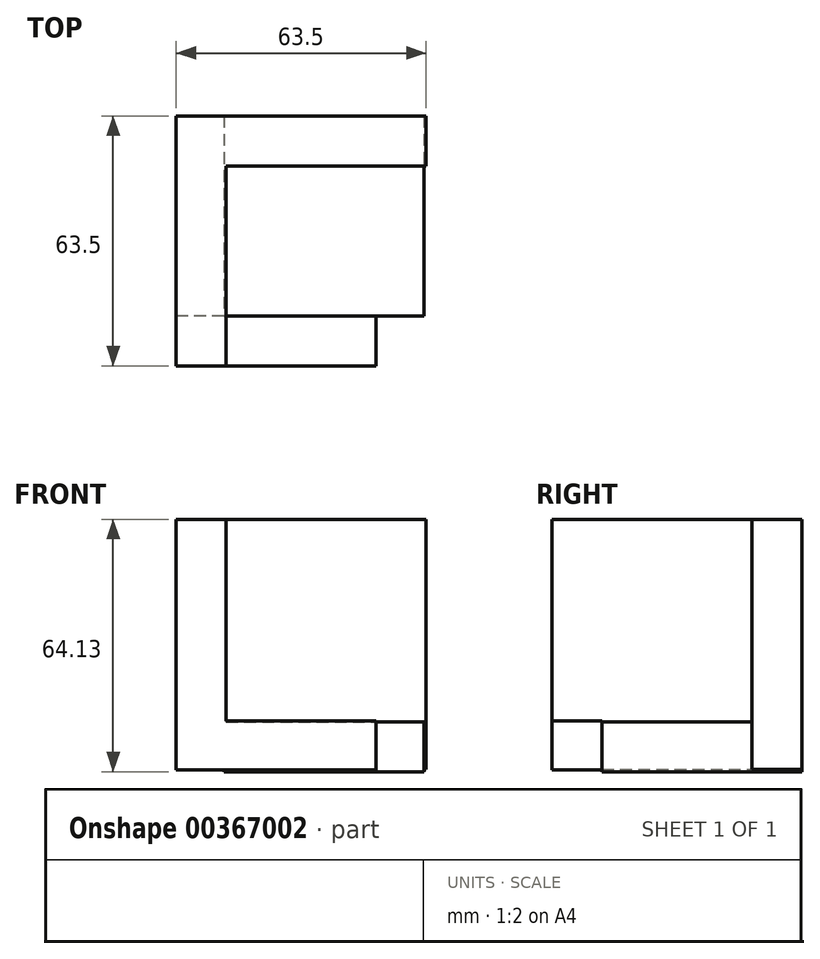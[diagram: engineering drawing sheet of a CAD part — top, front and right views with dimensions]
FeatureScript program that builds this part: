
annotation { "Feature Type Name" : "Feature", "Feature Type Description" : "" }
export const myFeature = defineFeature(function(context is Context, id is Id, definition is map)
    precondition{}
    {
        {
            var Q0;
            Q0=qCreatedBy(makeId("Front.planeOp"),FACE);
            var sketch = newSketch(context, id + "F0", { "sketchPlane" : qUnion([Q0])});
            skLineSegment(sketch, "E0.bottom", {"start": v(0, 0) * mm, "end": v(12.7, 0) * mm});
            skLineSegment(sketch, "E0.top", {"start": v(0, -63.5) * mm, "end": v(12.7, -63.5) * mm});
            skLineSegment(sketch, "E0.left", {"start": v(0, 0) * mm, "end": v(0, -63.5) * mm});
            skLineSegment(sketch, "E0.right", {"start": v(12.7, 0) * mm, "end": v(12.7, -63.5) * mm});
            skSolve(sketch);
        }
        {
            var Q0;
            Q0=makeQuery(id+"F0.imprint","IMPRINT",FACE,{"disambiguationData":[TD([[makeQuery(id+"F0.imprint","IMPRINT",EDGE,{"derivedFrom":sQuery(id+"F0.wireOp",EDGE,"E0.bottom")}),-1.0]])]});
            extrude(context, id + "F1", {"entities" : qUnion([Q0]), "depth" : 63.5 * mm});
        }
        {
            var Q0;
            Q0=qCreatedBy(makeId("Right.planeOp"),FACE);
            var sketch = newSketch(context, id + "F2", { "sketchPlane" : qUnion([Q0])});
            skLineSegment(sketch, "E1.bottom", {"start": v(0, 0) * mm, "end": v(-12.7, 0) * mm});
            skLineSegment(sketch, "E1.top", {"start": v(0, -63.5) * mm, "end": v(-12.7, -63.5) * mm});
            skLineSegment(sketch, "E1.left", {"start": v(0, 0) * mm, "end": v(0, -63.5) * mm});
            skLineSegment(sketch, "E1.right", {"start": v(-12.7, 0) * mm, "end": v(-12.7, -63.5) * mm});
            skSolve(sketch);
        }
        {
            var Q0;
            Q0=makeQuery(id+"F2.imprint","IMPRINT",FACE,{"disambiguationData":[TD([[makeQuery(id+"F2.imprint","IMPRINT",EDGE,{"derivedFrom":sQuery(id+"F2.wireOp",EDGE,"E1.bottom")}),1.0]])]});
            extrude(context, id + "F3", {"entities" : qUnion([Q0]), "operationType" : NewBodyOperationType.ADD, "depth" : 63.5 * mm});
        }
        {
            var Q0;
            Q0=qCreatedBy(makeId("Front.planeOp"),FACE);
            var sketch = newSketch(context, id + "F4", { "sketchPlane" : qUnion([Q0])});
            skLineSegment(sketch, "E2.bottom", {"start": v(12.17, -64.13) * mm, "end": v(62.97, -64.13) * mm});
            skLineSegment(sketch, "E2.top", {"start": v(12.17, -51.43) * mm, "end": v(62.97, -51.43) * mm});
            skLineSegment(sketch, "E2.left", {"start": v(12.17, -64.13) * mm, "end": v(12.17, -51.43) * mm});
            skLineSegment(sketch, "E2.right", {"start": v(62.97, -64.13) * mm, "end": v(62.97, -51.43) * mm});
            skSolve(sketch);
        }
        {
            var Q0;
            Q0=makeQuery(id+"F4.imprint","IMPRINT",FACE,{"disambiguationData":[TD([[makeQuery(id+"F4.imprint","IMPRINT",EDGE,{"derivedFrom":sQuery(id+"F4.wireOp",EDGE,"E2.bottom")}),1.0]])]});
            extrude(context, id + "F5", {"entities" : qUnion([Q0]), "operationType" : NewBodyOperationType.ADD, "depth" : 50.8 * mm});
        }
        {
            var Q0;
            Q0=qCreatedBy(makeId("Right.planeOp"),FACE);
            var sketch = newSketch(context, id + "F6", { "sketchPlane" : qUnion([Q0])});
            skLineSegment(sketch, "E3.bottom", {"start": v(-63.5, -51.3) * mm, "end": v(-50.8, -51.3) * mm});
            skLineSegment(sketch, "E3.top", {"start": v(-63.5, -63.66) * mm, "end": v(-50.8, -63.66) * mm});
            skLineSegment(sketch, "E3.left", {"start": v(-63.5, -51.3) * mm, "end": v(-63.5, -63.66) * mm});
            skLineSegment(sketch, "E3.right", {"start": v(-50.8, -51.3) * mm, "end": v(-50.8, -63.66) * mm});
            skSolve(sketch);
        }
        {
            var Q0;
            Q0=makeQuery(id+"F6.imprint","IMPRINT",FACE,{"disambiguationData":[TD([[makeQuery(id+"F6.imprint","IMPRINT",EDGE,{"derivedFrom":sQuery(id+"F6.wireOp",EDGE,"E3.bottom")}),-1.0]])]});
            extrude(context, id + "F7", {"entities" : qUnion([Q0]), "operationType" : NewBodyOperationType.ADD, "depth" : 50.8 * mm});
        }
    });
